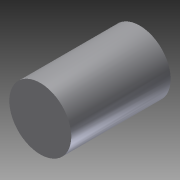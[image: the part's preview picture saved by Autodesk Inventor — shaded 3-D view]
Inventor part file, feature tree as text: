
AUTODESK INVENTOR PART (.ipt)
format: ipt  version: 2014 (Build 180170000, 170)  size: 83,456 bytes
history: native  units: in
note: dims shown in document units (in); Inventor stores cm internally (conversion verified against a paired STEP export)
features: plane x1, extrude x1, sketch x1, reference x1
ambient origin geometry x8: Origin, YZ Plane, XZ Plane, XY Plane, X Axis, Y Axis, Z Axis, Center Point
bodies: Solid1 (feature_tree)
feature tree (4):
  plane  "Work Plane1"
  extrude  "Extrusion1"  Depth=3.358in TaperAngle=0.0deg
  sketch  "Sketch1"  dims[d0=2.11in d1=3.358in d2=0.0in]
  reference  "Reference1"
